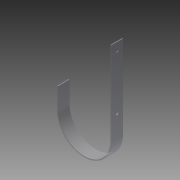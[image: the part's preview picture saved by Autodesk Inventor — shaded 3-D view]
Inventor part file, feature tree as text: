
AUTODESK INVENTOR PART (.ipt)
format: ipt  version: 2014 SP1 (Build 180222100, 222)  size: 106,496 bytes
history: native  units: in
note: dims shown in document units (in); Inventor stores cm internally (conversion verified against a paired STEP export)
features: sketch x3, extrude x2, other x1, projected_geometry x1
ambient origin geometry x8: Origin, YZ Plane, XZ Plane, XY Plane, X Axis, Y Axis, Z Axis, Center Point
bodies: Solid1 (feature_tree)
feature tree (7):
  extrude  "Extrusion1"  Depth=0.75in
  other  "Bend Part2"
  extrude  "Extrusion2"  Depth=4.0in
  sketch  "Sketch1"  dims[d0=0.75in d1=12.0in]
  sketch  "Sketch2"  dims[d2=0.0625in d3=0.0in d4=4.0in]
  projected_geometry  "Projected Loop1"
  sketch  "Sketch3"  dims[d7=180.0deg d8=5.3in d9=0.175in d10=0.5in d11=0.7874in d13=3.5in d14=0.3937in d16=1.0in d18=0.0625in d19=0.0in]
